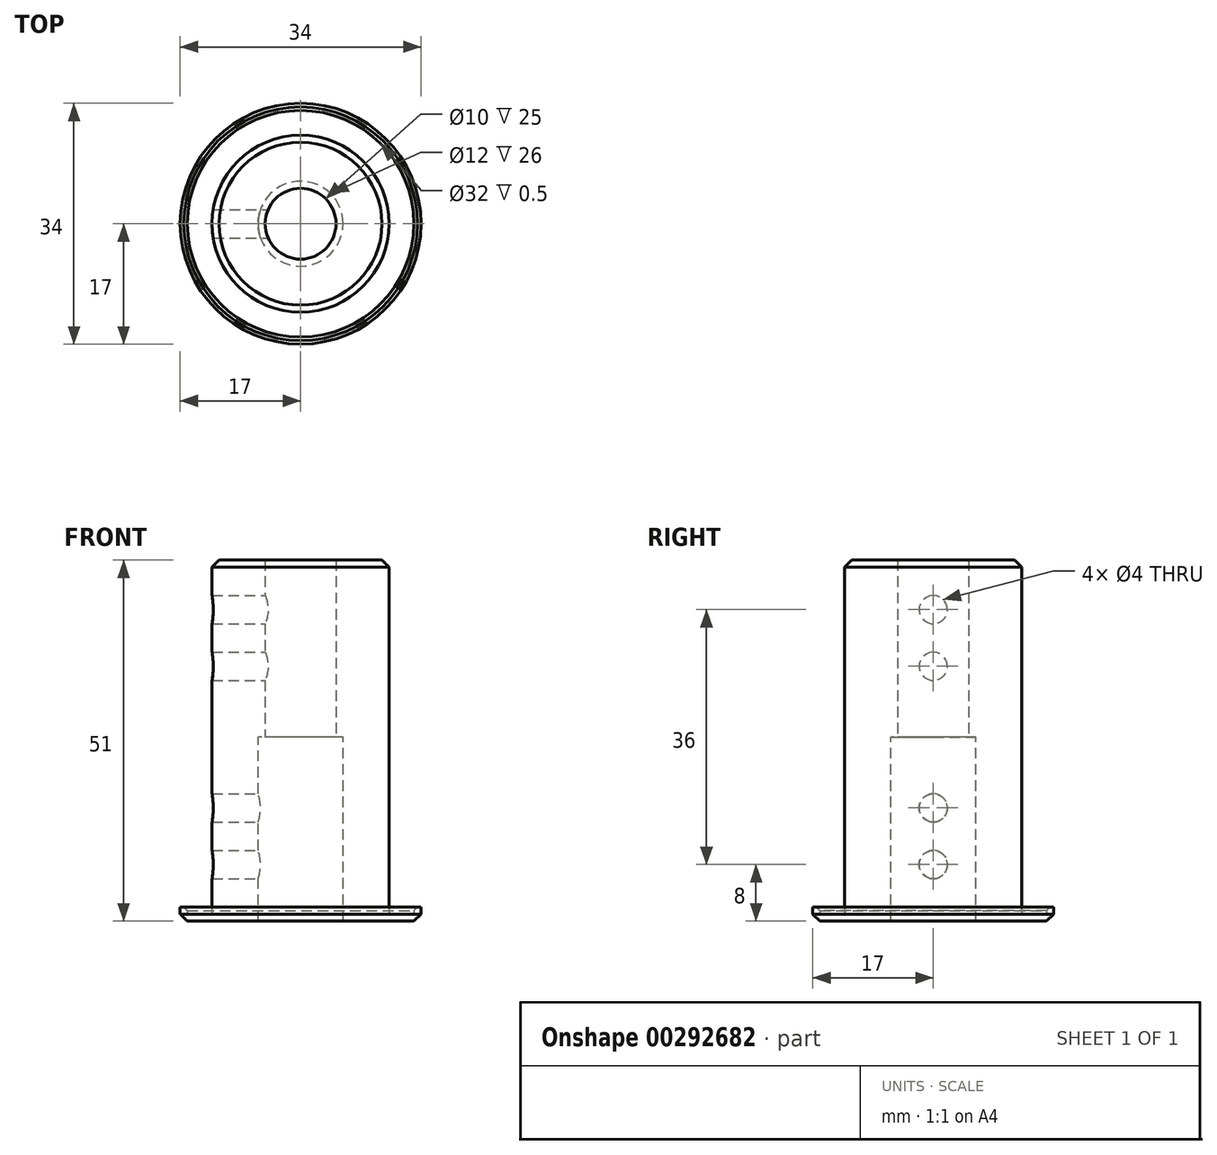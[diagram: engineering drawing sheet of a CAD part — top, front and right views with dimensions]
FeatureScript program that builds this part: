
annotation { "Feature Type Name" : "Feature", "Feature Type Description" : "" }
export const myFeature = defineFeature(function(context is Context, id is Id, definition is map)
    precondition{}
    {
        {
            var Q0;
            Q0=qCreatedBy(makeId("Top.planeOp"),FACE);
            var sketch = newSketch(context, id + "F0", { "sketchPlane" : qUnion([Q0])});
            skCircle(sketch, "E0", {"center": v(0, 0) * mm, "radius": 6 * mm});
            skCircle(sketch, "E1", {"center": v(0, 0) * mm, "radius": 5 * mm});
            skCircle(sketch, "E2", {"center": v(0, 0) * mm, "radius": 12.5 * mm});
            skSolve(sketch);
        }
        {
            var Q0;
            Q0=makeQuery(id+"F0.imprint","IMPRINT",FACE,{"disambiguationData":[TD([[makeQuery(id+"F0.imprint","IMPRINT",EDGE,{"derivedFrom":sQuery(id+"F0.wireOp",EDGE,"E0")}),-1.0]])]});
            var Q1;
            Q1=makeQuery(id+"F0.imprint","IMPRINT",FACE,{"disambiguationData":[TD([[makeQuery(id+"F0.imprint","IMPRINT",EDGE,{"derivedFrom":sQuery(id+"F0.wireOp",EDGE,"E0")}),1.0]])]});
            extrude(context, id + "F1", {"entities" : qUnion([Q0, Q1]), "depth" : 25 * mm, "offsetDistance" : 25 * mm});
        }
        {
            var Q0;
            Q0=makeQuery(id+"F0.imprint","IMPRINT",FACE,{"disambiguationData":[TD([[makeQuery(id+"F0.imprint","IMPRINT",EDGE,{"derivedFrom":sQuery(id+"F0.wireOp",EDGE,"E0")}),-1.0]])]});
            extrude(context, id + "F2", {"entities" : qUnion([Q0]), "operationType" : NewBodyOperationType.ADD, "oppositeDirection" : true, "depth" : 25 * mm, "offsetDistance" : 25 * mm});
        }
        {
            var Q0;
            Q0=qCreatedBy(makeId("Right.planeOp"),FACE);
            var sketch = newSketch(context, id + "F3", { "sketchPlane" : qUnion([Q0])});
            skCircle(sketch, "E3", {"center": v(0, -18) * mm, "radius": 2 * mm});
            skCircle(sketch, "E4", {"center": v(0, -10) * mm, "radius": 2 * mm});
            skCircle(sketch, "E5", {"center": v(0, 10) * mm, "radius": 2 * mm});
            skCircle(sketch, "E6", {"center": v(0, 18) * mm, "radius": 2 * mm});
            skSolve(sketch);
        }
        {
            var Q0;
            Q0 = qSketchRegion(id + "F3", true);
            extrude(context, id + "F4", {"entities" : qUnion([Q0]), "operationType" : NewBodyOperationType.REMOVE, "oppositeDirection" : true, "depth" : 25 * mm, "offsetDistance" : 25 * mm});
        }
        {
            var Q0;
            Q0=makeQuery(id+"F1.opExtrude","CAP_EDGE",EDGE,{"disambiguationData":[OSD([sQuery(id+"F0.wireOp",EDGE,"E2")])],"isStart":false});
            chamfer(context, id + "F5", {"entities" : qUnion([Q0]), "width" : 1 * mm, "tangentPropagation" : true});
        }
        {
            var Q0;
            Q0=makeQuery(id+"F2.opExtrude","CAP_FACE",FACE,{"disambiguationData":[OSD([sQuery(id+"F0.wireOp",EDGE,"E0"),sQuery(id+"F0.wireOp",EDGE,"E2")])],"isStart":false});
            var sketch = newSketch(context, id + "F6", { "sketchPlane" : qUnion([Q0])});
            skCircle(sketch, "E7", {"center": v(0, 0) * mm, "radius": 16 * mm});
            skCircle(sketch, "E8", {"center": v(0, 0) * mm, "radius": 17 * mm});
            skSolve(sketch);
        }
        {
            var Q0;
            Q0=makeQuery(id+"F6.imprint","IMPRINT",FACE,{"disambiguationData":[TD([[makeQuery(id+"F6.imprint","IMPRINT",EDGE,{"derivedFrom":sQuery(id+"F6.wireOp",EDGE,"E7")}),1.0]])]});
            var Q1;
            Q1=makeQuery(id+"F6.imprint","IMPRINT",FACE,{"disambiguationData":[TD([[makeQuery(id+"F6.imprint","IMPRINT",EDGE,{"derivedFrom":sQuery(id+"F6.wireOp",EDGE,"E7")}),-1.0]])]});
            var Q2;
            Q2=makeQuery(id+"F6.imprint","IMPRINT",FACE,{"disambiguationData":[TD([[makeQuery(id+"F6.imprint","IMPRINT",EDGE,{"derivedFrom":makeQuery(id+"F2.opExtrude","CAP_EDGE",EDGE,{"disambiguationData":[OSD([sQuery(id+"F0.wireOp",EDGE,"E0")])],"isStart":false})}),1.0]])]});
            extrude(context, id + "F7", {"entities" : qUnion([Q0, Q1, Q2]), "operationType" : NewBodyOperationType.ADD, "depth" : 1 * mm, "offsetDistance" : 25 * mm});
        }
        {
            var Q0;
            Q0=makeQuery(id+"F6.imprint","IMPRINT",FACE,{"disambiguationData":[TD([[makeQuery(id+"F6.imprint","IMPRINT",EDGE,{"derivedFrom":sQuery(id+"F6.wireOp",EDGE,"E7")}),-1.0]])]});
            extrude(context, id + "F8", {"entities" : qUnion([Q0]), "operationType" : NewBodyOperationType.ADD, "oppositeDirection" : true, "depth" : 1 * mm, "offsetDistance" : 25 * mm});
        }
        {
            var Q0;
            Q0=makeQuery(id+"F8.opExtrude","CAP_EDGE",EDGE,{"disambiguationData":[OSD([sQuery(id+"F6.wireOp",EDGE,"E7")])],"isStart":false});
            chamfer(context, id + "F9", {"entities" : qUnion([Q0]), "width" : 0.5 * mm, "tangentPropagation" : true});
        }
        {
            var Q0;
            Q0=makeQuery(id+"F7.opExtrude","CAP_EDGE",EDGE,{"disambiguationData":[OSD([sQuery(id+"F6.wireOp",EDGE,"E8")])],"isStart":false});
            chamfer(context, id + "F10", {"entities" : qUnion([Q0]), "width" : 1 * mm, "tangentPropagation" : true});
        }
    });
